# Revit family: Domotics-DomesticRanges-GEWISS-SYSTEM_SIGNALLING-LAMP_STAIR_RISER_PROTRUDING_2M
name_source: partatom
category: Apparecchi elettrici
revit_build: Autodesk Revit 2016 (Build: 20161004_0715(x64)
units: mm (PartAtom-declared; Revit-internal decimal feet)

## family parameters
Condiviso = Sì
Host = Superficie
Mantenere orientamento annotazione = Sì
Punto di calcolo locali = Sì
Quota connettore circolare = Usa diametro
Taglio con vuoti quando caricato = No
Tipo di parte = Normale

## types (5) — shared parameters
Catalogue = DOMOTICS
Catalogue Range = SYSTEM - DOMESTIC RANGE
Description. = Protruding stair riser lamp
Electrocod = 0132
Fixing for lamp = Cartridge
IDF = cef270f9-311f-4c14-a462-7409770b47ca
IDT = 59665550-0299-48c5-9512-d4a7e45699d2
Immagine tipo = GW20630.jpg
Lamp holder = Cartridge
No. SYSTEM modules = 3
Produttore = GEWISS S.p.A.
Prospetto di default = 1219 mm
SEO = Lamp
Technical sheet = https://www.gewiss.com
Tipo_ = System Spie Segnapasso_G_SP : GW20630 Spia segnapasso con diffusore piano azzurro
URL = https://www.gewiss.com
Version file RFA = 19.4
Voltage = 12/24V AC
Voltage: = 12/24V AC

## per-type parameters (varying)
| type | Descrizione | Diffuser colour | Diffuser colour: | EAN code | Modello |
| GW20627 - Red protruding stair riser lamp | RED PROTRUDING STAIR RISER LAMP | Red | Red | 8011564024779 | GW20627 |
| GW20630 - Blue protruding stair riser lamp | BLUE PROTRUDING STAIR RISER LAMP | Light blue | Light blue | 8011564024731 | GW20630 |
| GW20628 - Green protruding stair riser lamp | GREEN PROTRUDING STAIR RISER LAMP | Green | Green | 8011564024762 | GW20628 |
| GW20602 - Opal protruding stair riser lamp | OPAL PROTRUDING STAIR RISER LAMP | Opal | Opal | 8011564001046 | GW20602 |
| GW20629 - Yellow protruding stair riser lamp | YELLOW PROTRUDING STAIR RISER LAMP | Yellow | Yellow | 8011564024755 | GW20629 |

## geometry (parser evidence)
native form markers: Sweep x1
no freeform markers — native parametric forms only
